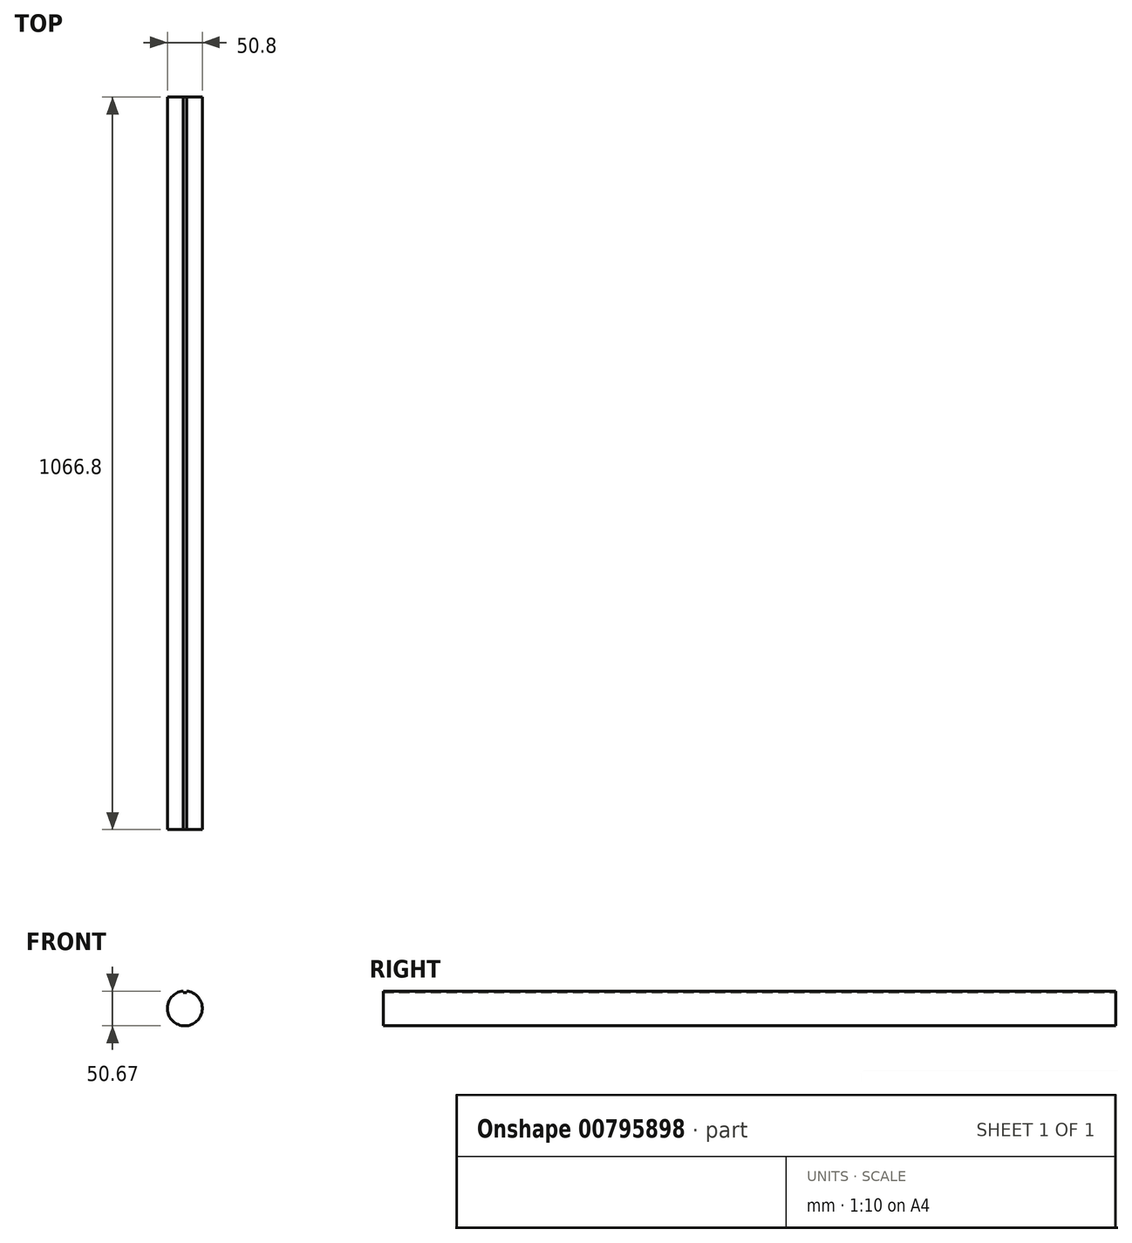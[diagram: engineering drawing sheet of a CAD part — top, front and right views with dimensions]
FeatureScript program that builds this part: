
annotation { "Feature Type Name" : "Feature", "Feature Type Description" : "" }
export const myFeature = defineFeature(function(context is Context, id is Id, definition is map)
    precondition{}
    {
        {
            var Q0;
            Q0=qCreatedBy(makeId("Front.planeOp"),FACE);
            var sketch = newSketch(context, id + "F0", { "sketchPlane" : qUnion([Q0])});
            skArc(sketch, "E0", {"start": v(-2.54, 25.27) * mm, "mid": v(0, -25.4) * mm, "end": v(2.54, 25.27) * mm});
            skLineSegment(sketch, "E1.top", {"start": v(-2.54, 22.86) * mm, "end": v(2.54, 22.86) * mm});
            skLineSegment(sketch, "E1.left", {"start": v(-2.54, 25.27) * mm, "end": v(-2.54, 22.86) * mm});
            skLineSegment(sketch, "E1.right", {"start": v(2.54, 25.27) * mm, "end": v(2.54, 22.86) * mm});
            skPoint(sketch, "E1.middle", {"position": v(0, 25.4) * mm});
            skPoint(sketch, "E2.orphan", {"position": v(2.54, 27.94) * mm});
            skPoint(sketch, "E3.orphan", {"position": v(-2.54, 27.94) * mm});
            skSolve(sketch);
        }
        {
            var Q0;
            Q0 = qSketchRegion(id + "F0", true);
            extrude(context, id + "F1", {"entities" : qUnion([Q0]), "endBound" : BoundingType.SYMMETRIC, "depth" : 1066.8 * mm, "offsetDistance" : 25.4 * mm});
        }
    });
